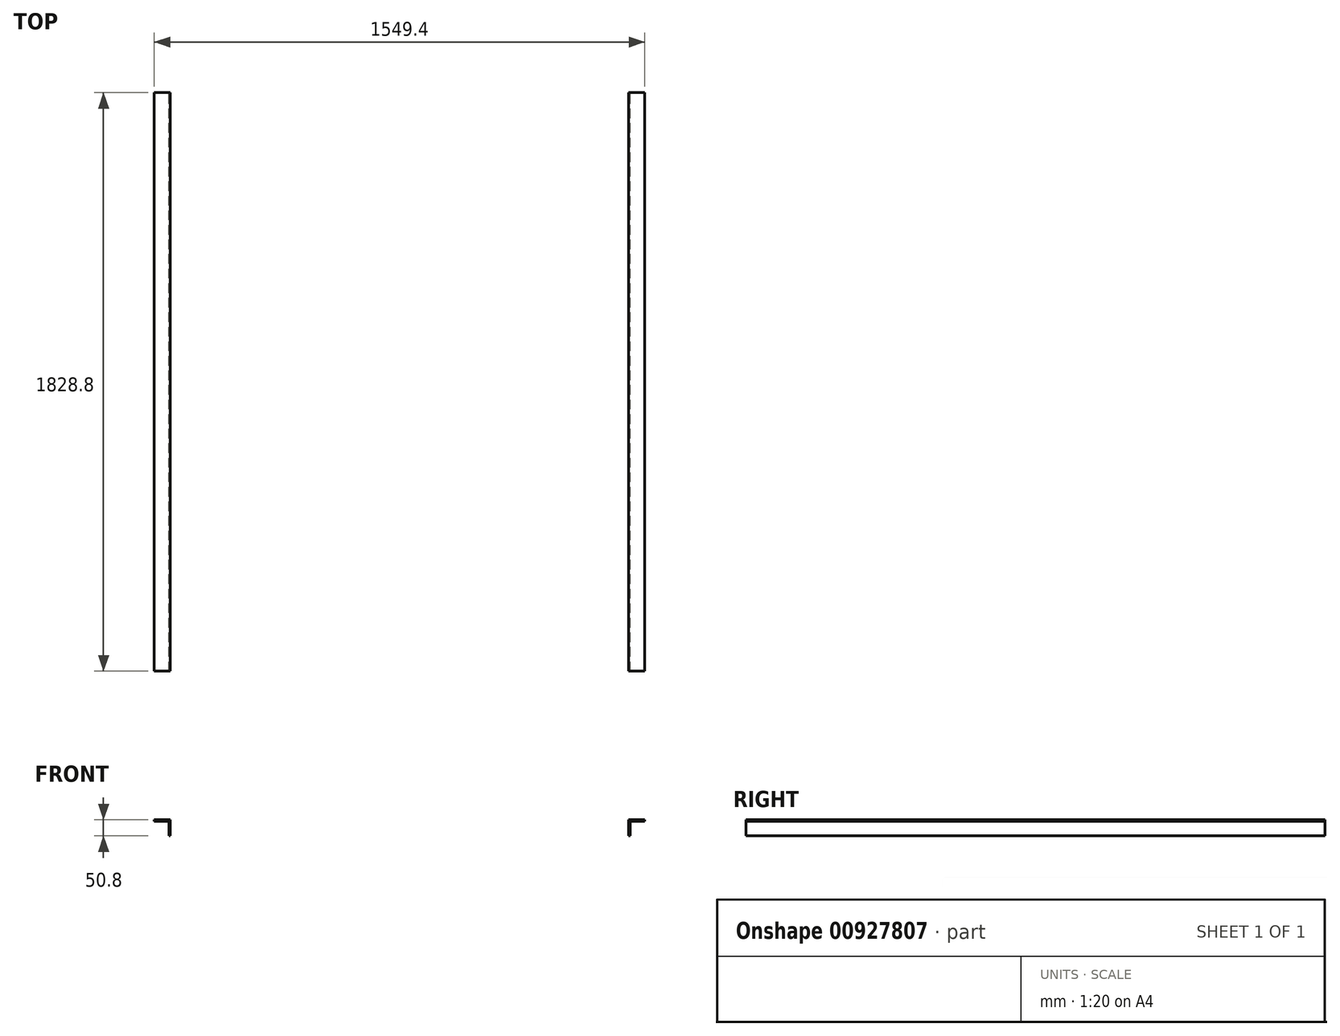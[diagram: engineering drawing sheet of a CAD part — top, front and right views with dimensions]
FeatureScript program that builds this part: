
annotation { "Feature Type Name" : "Feature", "Feature Type Description" : "" }
export const myFeature = defineFeature(function(context is Context, id is Id, definition is map)
    precondition{}
    {
        {
            var Q0;
            Q0=qCreatedBy(makeId("Front.planeOp"),FACE);
            var sketch = newSketch(context, id + "F0", { "sketchPlane" : qUnion([Q0])});
            skLineSegment(sketch, "E0", {"start": v(-723.9, -27.4) * mm, "end": v(-723.9, 23.4) * mm});
            skLineSegment(sketch, "E1", {"start": v(-723.9, 23.4) * mm, "end": v(-774.7, 23.4) * mm});
            skLineSegment(sketch, "E2", {"start": v(-774.7, 23.4) * mm, "end": v(-774.7, 18.96) * mm});
            skLineSegment(sketch, "E3", {"start": v(-774.7, 18.96) * mm, "end": v(-723.9, 18.96) * mm});
            skLineSegment(sketch, "E4", {"start": v(-723.9, -27.4) * mm, "end": v(-728.35, -27.4) * mm});
            skLineSegment(sketch, "E5", {"start": v(-728.35, -27.4) * mm, "end": v(-728.35, 23.4) * mm});
            skLineSegment(sketch, "E6.MirrorCS", {"start": v(723.9, 23.4) * mm, "end": v(774.7, 23.4) * mm});
            skLineSegment(sketch, "E7.MirrorCS", {"start": v(728.35, -27.4) * mm, "end": v(728.35, 23.4) * mm});
            skLineSegment(sketch, "E8.MirrorCS", {"start": v(723.9, -27.4) * mm, "end": v(723.9, 23.4) * mm});
            skLineSegment(sketch, "E9.MirrorCS", {"start": v(723.9, -27.4) * mm, "end": v(728.35, -27.4) * mm});
            skLineSegment(sketch, "E10.MirrorCS", {"start": v(774.7, 18.96) * mm, "end": v(723.9, 18.96) * mm});
            skLineSegment(sketch, "E11.MirrorCS", {"start": v(774.7, 23.4) * mm, "end": v(774.7, 18.96) * mm});
            skSolve(sketch);
        }
        {
            var Q0;
            Q0 = qSketchRegion(id + "F0", true);
            extrude(context, id + "F1", {"entities" : qUnion([Q0]), "depth" : 1828.8 * mm, "offsetDistance" : 25.4 * mm});
        }
    });
